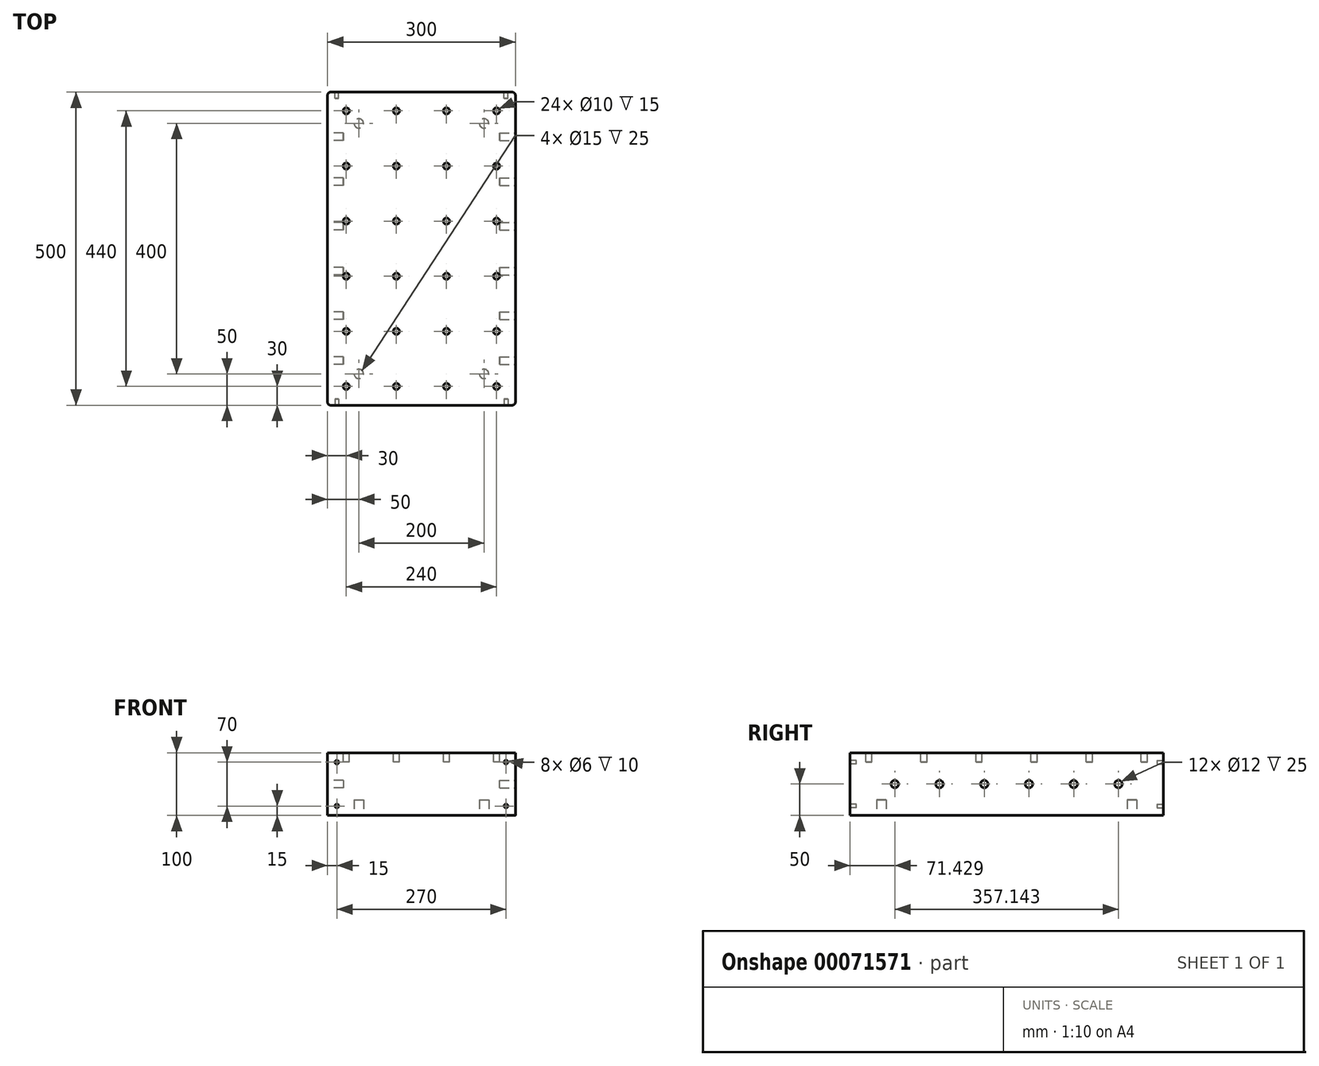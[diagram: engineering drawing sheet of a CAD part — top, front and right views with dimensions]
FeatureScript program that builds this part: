
annotation { "Feature Type Name" : "Feature", "Feature Type Description" : "" }
export const myFeature = defineFeature(function(context is Context, id is Id, definition is map)
    precondition{}
    {
        {
            var Q0;
            Q0=qCreatedBy(makeId("Top.planeOp"),FACE);
            var sketch = newSketch(context, id + "F0", { "sketchPlane" : qUnion([Q0])});
            skLineSegment(sketch, "E0.rect.bottom", {"start": v(-150, -250) * mm, "end": v(150, -250) * mm});
            skLineSegment(sketch, "E0.rect.top", {"start": v(-150, 250) * mm, "end": v(150, 250) * mm});
            skLineSegment(sketch, "E0.rect.left", {"start": v(-150, -250) * mm, "end": v(-150, 250) * mm});
            skLineSegment(sketch, "E0.rect.right", {"start": v(150, -250) * mm, "end": v(150, 250) * mm});
            skPoint(sketch, "E0.rect.middle", {"position": v(0, 0) * mm});
            skSolve(sketch);
        }
        {
            var Q0;
            Q0 = qSketchRegion(id + "F0", true);
            extrude(context, id + "F1", {"entities" : qUnion([Q0]), "depth" : 100 * mm});
        }
        {
            var Q0;
            Q0=makeQuery(id+"F1.opExtrude","CAP_FACE",FACE,{"disambiguationData":[OSD([sQuery(id+"F0.wireOp",EDGE,"E0.rect.bottom"),sQuery(id+"F0.wireOp",EDGE,"E0.rect.top"),sQuery(id+"F0.wireOp",EDGE,"E0.rect.left"),sQuery(id+"F0.wireOp",EDGE,"E0.rect.right")])],"isStart":true});
            var sketch = newSketch(context, id + "F2", { "sketchPlane" : qUnion([Q0])});
            skLineSegment(sketch, "E1.rect.bottom", {"start": v(-100, 200) * mm, "end": v(100, 200) * mm, "construction": true});
            skLineSegment(sketch, "E1.rect.top", {"start": v(-100, -200) * mm, "end": v(100, -200) * mm, "construction": true});
            skLineSegment(sketch, "E1.rect.left", {"start": v(-100, 200) * mm, "end": v(-100, -200) * mm, "construction": true});
            skLineSegment(sketch, "E1.rect.right", {"start": v(100, 200) * mm, "end": v(100, -200) * mm, "construction": true});
            skPoint(sketch, "E1.rect.middle", {"position": v(0, 0) * mm});
            skCircle(sketch, "E2", {"center": v(-100, 200) * mm, "radius": 7.5 * mm});
            skCircle(sketch, "E3", {"center": v(100, 200) * mm, "radius": 7.5 * mm});
            skCircle(sketch, "E4", {"center": v(100, -200) * mm, "radius": 7.5 * mm});
            skCircle(sketch, "E5", {"center": v(-100, -200) * mm, "radius": 7.5 * mm});
            skSolve(sketch);
        }
        {
            var Q0;
            Q0=qCreatedBy(makeId("Front.planeOp"),FACE);
            var sketch = newSketch(context, id + "F3", { "sketchPlane" : qUnion([Q0])});
            skLineSegment(sketch, "E6", {"start": v(150, 82.5) * mm, "end": v(150, 17.5) * mm});
            skLineSegment(sketch, "E7", {"start": v(150, 17.5) * mm, "end": v(120, 17.5) * mm});
            skLineSegment(sketch, "E8", {"start": v(120, 17.5) * mm, "end": v(120, 32.5) * mm});
            skLineSegment(sketch, "E9", {"start": v(120, 32.5) * mm, "end": v(140, 32.5) * mm});
            skLineSegment(sketch, "E10", {"start": v(140, 32.5) * mm, "end": v(140, 67.5) * mm});
            skLineSegment(sketch, "E11", {"start": v(140, 67.5) * mm, "end": v(120, 67.5) * mm});
            skLineSegment(sketch, "E12", {"start": v(120, 67.5) * mm, "end": v(120, 82.5) * mm});
            skLineSegment(sketch, "E13", {"start": v(120, 82.5) * mm, "end": v(150, 82.5) * mm});
            skLineSegment(sketch, "E14", {"start": v(150, 50) * mm, "end": v(120, 50) * mm, "construction": true});
            skLineSegment(sketch, "E15", {"start": v(120, 50) * mm, "end": v(120, 67.5) * mm, "construction": true});
            skLineSegment(sketch, "E16", {"start": v(120, 50) * mm, "end": v(120, 32.5) * mm, "construction": true});
            skLineSegment(sketch, "E17", {"start": v(0, 0) * mm, "end": v(0, 100) * mm, "construction": true});
            skLineSegment(sketch, "E18.MirrorCS", {"start": v(-150, 82.5) * mm, "end": v(-150, 17.5) * mm});
            skLineSegment(sketch, "E19.MirrorCS", {"start": v(-120, 50) * mm, "end": v(-120, 32.5) * mm, "construction": true});
            skLineSegment(sketch, "E20.MirrorCS", {"start": v(-140, 32.5) * mm, "end": v(-140, 67.5) * mm});
            skLineSegment(sketch, "E21.MirrorCS", {"start": v(-140, 67.5) * mm, "end": v(-120, 67.5) * mm});
            skLineSegment(sketch, "E22.MirrorCS", {"start": v(-120, 32.5) * mm, "end": v(-140, 32.5) * mm});
            skLineSegment(sketch, "E23.MirrorCS", {"start": v(-120, 82.5) * mm, "end": v(-150, 82.5) * mm});
            skLineSegment(sketch, "E24.MirrorCS", {"start": v(-120, 17.5) * mm, "end": v(-120, 32.5) * mm});
            skLineSegment(sketch, "E25.MirrorCS", {"start": v(-120, 67.5) * mm, "end": v(-120, 82.5) * mm});
            skLineSegment(sketch, "E26.MirrorCS", {"start": v(-150, 50) * mm, "end": v(-120, 50) * mm, "construction": true});
            skLineSegment(sketch, "E27.MirrorCS", {"start": v(-120, 50) * mm, "end": v(-120, 67.5) * mm, "construction": true});
            skLineSegment(sketch, "E28.MirrorCS", {"start": v(-150, 17.5) * mm, "end": v(-120, 17.5) * mm});
            skSolve(sketch);
        }
        {
            var Q0;
            Q0 = qSketchRegion(id + "F3", true);
            extrude(context, id + "F4", {"entities" : qUnion([Q0]), "operationType" : NewBodyOperationType.REMOVE, "oppositeDirection" : true, "depth" : 225 * mm, "hasSecondDirection" : true, "secondDirectionOppositeDirection" : false, "secondDirectionDepth" : 225 * mm});
        }
        {
            var Q0;
            Q0 = qSketchRegion(id + "F3", true);
            extrude(context, id + "F5", {"entities" : qUnion([Q0]), "operationType" : NewBodyOperationType.ADD, "depth" : 225 * mm, "hasSecondDirection" : true, "secondDirectionOppositeDirection" : true, "secondDirectionDepth" : 225 * mm});
        }
        {
            var Q0;
            Q0 = qSketchRegion(id + "F2", true);
            extrude(context, id + "F6", {"entities" : qUnion([Q0]), "operationType" : NewBodyOperationType.REMOVE, "oppositeDirection" : true, "depth" : 25 * mm});
        }
        {
            var Q0;
            Q0=makeQuery(id+"F1.opExtrude","SWEPT_FACE",FACE,{"disambiguationData":[OSD([sQuery(id+"F0.wireOp",EDGE,"E0.rect.left")])]});
            var sketch = newSketch(context, id + "F7", { "sketchPlane" : qUnion([Q0])});
            skLineSegment(sketch, "E29", {"start": v(-250, 50) * mm, "end": v(-178.57, 50) * mm, "construction": true});
            skLineSegment(sketch, "E30", {"start": v(-178.57, 50) * mm, "end": v(-107.14, 50) * mm, "construction": true});
            skLineSegment(sketch, "E31", {"start": v(-107.14, 50) * mm, "end": v(-35.71, 50) * mm, "construction": true});
            skLineSegment(sketch, "E32", {"start": v(-35.71, 50) * mm, "end": v(35.71, 50) * mm, "construction": true});
            skLineSegment(sketch, "E33", {"start": v(35.71, 50) * mm, "end": v(107.14, 50) * mm, "construction": true});
            skLineSegment(sketch, "E34", {"start": v(107.14, 50) * mm, "end": v(178.57, 50) * mm, "construction": true});
            skLineSegment(sketch, "E35", {"start": v(178.57, 50) * mm, "end": v(250, 50) * mm, "construction": true});
            skCircle(sketch, "E36", {"center": v(-178.57, 50) * mm, "radius": 6 * mm});
            skCircle(sketch, "E37", {"center": v(-107.14, 50) * mm, "radius": 6 * mm});
            skCircle(sketch, "E38", {"center": v(-35.71, 50) * mm, "radius": 6 * mm});
            skCircle(sketch, "E39", {"center": v(35.71, 50) * mm, "radius": 6 * mm});
            skCircle(sketch, "E40", {"center": v(107.14, 50) * mm, "radius": 6 * mm});
            skCircle(sketch, "E41", {"center": v(178.57, 50) * mm, "radius": 6 * mm});
            skSolve(sketch);
        }
        {
            var Q0;
            Q0 = qSketchRegion(id + "F7", true);
            extrude(context, id + "F8", {"entities" : qUnion([Q0]), "operationType" : NewBodyOperationType.REMOVE, "oppositeDirection" : true, "depth" : 25 * mm});
        }
        {
            var Q0;
            Q0=makeQuery(id+"F1.opExtrude","SWEPT_FACE",FACE,{"disambiguationData":[OSD([sQuery(id+"F0.wireOp",EDGE,"E0.rect.right")])]});
            var sketch = newSketch(context, id + "F9", { "sketchPlane" : qUnion([Q0])});
            skLineSegment(sketch, "E42", {"start": v(-250, 50) * mm, "end": v(-178.57, 50) * mm, "construction": true});
            skLineSegment(sketch, "E43", {"start": v(-178.57, 50) * mm, "end": v(-107.14, 50) * mm, "construction": true});
            skLineSegment(sketch, "E44", {"start": v(-107.14, 50) * mm, "end": v(-35.71, 50) * mm, "construction": true});
            skLineSegment(sketch, "E45", {"start": v(-35.71, 50) * mm, "end": v(35.71, 50) * mm, "construction": true});
            skLineSegment(sketch, "E46", {"start": v(35.71, 50) * mm, "end": v(107.14, 50) * mm, "construction": true});
            skLineSegment(sketch, "E47", {"start": v(107.14, 50) * mm, "end": v(178.57, 50) * mm, "construction": true});
            skLineSegment(sketch, "E48", {"start": v(178.57, 50) * mm, "end": v(250, 50) * mm, "construction": true});
            skCircle(sketch, "E49", {"center": v(-178.57, 50) * mm, "radius": 6 * mm});
            skCircle(sketch, "E50", {"center": v(-107.14, 50) * mm, "radius": 6 * mm});
            skCircle(sketch, "E51", {"center": v(-35.71, 50) * mm, "radius": 6 * mm});
            skCircle(sketch, "E52", {"center": v(35.71, 50) * mm, "radius": 6 * mm});
            skCircle(sketch, "E53", {"center": v(107.14, 50) * mm, "radius": 6 * mm});
            skCircle(sketch, "E54", {"center": v(178.57, 50) * mm, "radius": 6 * mm});
            skSolve(sketch);
        }
        {
            var Q0;
            Q0=makeQuery(id+"F9.imprint","IMPRINT",FACE,{"disambiguationData":[TD([[makeQuery(id+"F9.imprint","IMPRINT",EDGE,{"derivedFrom":sQuery(id+"F9.wireOp",EDGE,"E49")}),1.0]])]});
            var Q1;
            Q1=makeQuery(id+"F9.imprint","IMPRINT",FACE,{"disambiguationData":[TD([[makeQuery(id+"F9.imprint","IMPRINT",EDGE,{"derivedFrom":sQuery(id+"F9.wireOp",EDGE,"E50")}),1.0]])]});
            var Q2;
            Q2=makeQuery(id+"F9.imprint","IMPRINT",FACE,{"disambiguationData":[TD([[makeQuery(id+"F9.imprint","IMPRINT",EDGE,{"derivedFrom":sQuery(id+"F9.wireOp",EDGE,"E51")}),1.0]])]});
            var Q3;
            Q3=makeQuery(id+"F9.imprint","IMPRINT",FACE,{"disambiguationData":[TD([[makeQuery(id+"F9.imprint","IMPRINT",EDGE,{"derivedFrom":sQuery(id+"F9.wireOp",EDGE,"E52")}),1.0]])]});
            var Q4;
            Q4=makeQuery(id+"F9.imprint","IMPRINT",FACE,{"disambiguationData":[TD([[makeQuery(id+"F9.imprint","IMPRINT",EDGE,{"derivedFrom":sQuery(id+"F9.wireOp",EDGE,"E53")}),1.0]])]});
            var Q5;
            Q5=makeQuery(id+"F9.imprint","IMPRINT",FACE,{"disambiguationData":[TD([[makeQuery(id+"F9.imprint","IMPRINT",EDGE,{"derivedFrom":sQuery(id+"F9.wireOp",EDGE,"E54")}),1.0]])]});
            extrude(context, id + "F10", {"entities" : qUnion([Q0, Q1, Q2, Q3, Q4, Q5]), "operationType" : NewBodyOperationType.REMOVE, "oppositeDirection" : true, "depth" : 25 * mm});
        }
        {
            var Q0;
            Q0=makeQuery(id+"F1.opExtrude","SWEPT_FACE",FACE,{"disambiguationData":[OSD([sQuery(id+"F0.wireOp",EDGE,"E0.rect.top")])]});
            var sketch = newSketch(context, id + "F11", { "sketchPlane" : qUnion([Q0])});
            skLineSegment(sketch, "E55.bottom", {"start": v(-135, 85) * mm, "end": v(135, 85) * mm, "construction": true});
            skLineSegment(sketch, "E55.top", {"start": v(-135, 15) * mm, "end": v(135, 15) * mm, "construction": true});
            skLineSegment(sketch, "E55.left", {"start": v(-135, 85) * mm, "end": v(-135, 15) * mm, "construction": true});
            skLineSegment(sketch, "E55.right", {"start": v(135, 85) * mm, "end": v(135, 15) * mm, "construction": true});
            skCircle(sketch, "E56", {"center": v(-135, 85) * mm, "radius": 3 * mm});
            skCircle(sketch, "E57", {"center": v(-135, 15) * mm, "radius": 3 * mm});
            skCircle(sketch, "E58", {"center": v(135, 15) * mm, "radius": 3 * mm});
            skCircle(sketch, "E59", {"center": v(135, 85) * mm, "radius": 3 * mm});
            skLineSegment(sketch, "E60", {"start": v(-150, 50) * mm, "end": v(-135, 50) * mm, "construction": true});
            skLineSegment(sketch, "E61", {"start": v(0, 0) * mm, "end": v(0, 15) * mm, "construction": true});
            skLineSegment(sketch, "E62", {"start": v(135, 50) * mm, "end": v(150, 50) * mm, "construction": true});
            skSolve(sketch);
        }
        {
            var Q0;
            Q0 = qSketchRegion(id + "F11", true);
            extrude(context, id + "F12", {"entities" : qUnion([Q0]), "operationType" : NewBodyOperationType.REMOVE, "oppositeDirection" : true, "depth" : 10 * mm});
        }
        {
            var Q0;
            Q0=makeQuery(id+"F1.opExtrude","SWEPT_FACE",FACE,{"disambiguationData":[OSD([sQuery(id+"F0.wireOp",EDGE,"E0.rect.bottom")])]});
            var sketch = newSketch(context, id + "F13", { "sketchPlane" : qUnion([Q0])});
            skLineSegment(sketch, "E63.right", {"start": v(135, 85) * mm, "end": v(135, 15) * mm, "construction": true});
            skLineSegment(sketch, "E63.left", {"start": v(-135, 85) * mm, "end": v(-135, 15) * mm, "construction": true});
            skLineSegment(sketch, "E63.top", {"start": v(-135, 15) * mm, "end": v(135, 15) * mm, "construction": true});
            skLineSegment(sketch, "E63.bottom", {"start": v(-135, 85) * mm, "end": v(135, 85) * mm, "construction": true});
            skCircle(sketch, "E64", {"center": v(135, 85) * mm, "radius": 3 * mm});
            skCircle(sketch, "E65", {"center": v(135, 15) * mm, "radius": 3 * mm});
            skCircle(sketch, "E66", {"center": v(-135, 15) * mm, "radius": 3 * mm});
            skCircle(sketch, "E67", {"center": v(-135, 85) * mm, "radius": 3 * mm});
            skLineSegment(sketch, "E68", {"start": v(0, 85) * mm, "end": v(0, 100) * mm});
            skLineSegment(sketch, "E69", {"start": v(135, 50) * mm, "end": v(150, 50) * mm});
            skLineSegment(sketch, "E70", {"start": v(0, 0) * mm, "end": v(0, 15) * mm});
            skLineSegment(sketch, "E71", {"start": v(-135, 50) * mm, "end": v(-150, 50) * mm});
            skSolve(sketch);
        }
        {
            var Q0;
            Q0 = qSketchRegion(id + "F13", true);
            extrude(context, id + "F14", {"entities" : qUnion([Q0]), "operationType" : NewBodyOperationType.REMOVE, "oppositeDirection" : true, "depth" : 10 * mm});
        }
        {
            var Q0;
            Q0=makeQuery(id+"F1.opExtrude","CAP_FACE",FACE,{"disambiguationData":[OSD([sQuery(id+"F0.wireOp",EDGE,"E0.rect.bottom"),sQuery(id+"F0.wireOp",EDGE,"E0.rect.top"),sQuery(id+"F0.wireOp",EDGE,"E0.rect.left"),sQuery(id+"F0.wireOp",EDGE,"E0.rect.right")])],"isStart":false});
            var sketch = newSketch(context, id + "F15", { "sketchPlane" : qUnion([Q0])});
            skLineSegment(sketch, "E72.rect.bottom", {"start": v(-120, 220) * mm, "end": v(120, 220) * mm, "construction": true});
            skLineSegment(sketch, "E72.rect.top", {"start": v(-120, -220) * mm, "end": v(120, -220) * mm, "construction": true});
            skLineSegment(sketch, "E72.rect.left", {"start": v(-120, 220) * mm, "end": v(-120, -220) * mm, "construction": true});
            skLineSegment(sketch, "E72.rect.right", {"start": v(120, 220) * mm, "end": v(120, -220) * mm, "construction": true});
            skPoint(sketch, "E72.rect.middle", {"position": v(0, 0) * mm});
            skLineSegment(sketch, "E73", {"start": v(0, 220) * mm, "end": v(0, 250) * mm, "construction": true});
            skLineSegment(sketch, "E74", {"start": v(120, 0) * mm, "end": v(150, 0) * mm, "construction": true});
            skCircle(sketch, "E75", {"center": v(120, 220) * mm, "radius": 5 * mm});
            skCircle(sketch, "E76.0.1.0", {"center": v(120, 132) * mm, "radius": 5 * mm});
            skCircle(sketch, "E76.0.2.0", {"center": v(120, 44) * mm, "radius": 5 * mm});
            skCircle(sketch, "E76.0.3.0", {"center": v(120, -44) * mm, "radius": 5 * mm});
            skCircle(sketch, "E76.0.4.0", {"center": v(120, -132) * mm, "radius": 5 * mm});
            skCircle(sketch, "E76.0.5.0", {"center": v(120, -220) * mm, "radius": 5 * mm});
            skCircle(sketch, "E76.1.0.0", {"center": v(40, 220) * mm, "radius": 5 * mm});
            skCircle(sketch, "E76.1.1.0", {"center": v(40, 132) * mm, "radius": 5 * mm});
            skCircle(sketch, "E76.1.2.0", {"center": v(40, 44) * mm, "radius": 5 * mm});
            skCircle(sketch, "E76.1.3.0", {"center": v(40, -44) * mm, "radius": 5 * mm});
            skCircle(sketch, "E76.1.4.0", {"center": v(40, -132) * mm, "radius": 5 * mm});
            skCircle(sketch, "E76.1.5.0", {"center": v(40, -220) * mm, "radius": 5 * mm});
            skCircle(sketch, "E76.2.0.0", {"center": v(-40, 220) * mm, "radius": 5 * mm});
            skCircle(sketch, "E76.2.1.0", {"center": v(-40, 132) * mm, "radius": 5 * mm});
            skCircle(sketch, "E76.2.2.0", {"center": v(-40, 44) * mm, "radius": 5 * mm});
            skCircle(sketch, "E76.2.3.0", {"center": v(-40, -44) * mm, "radius": 5 * mm});
            skCircle(sketch, "E76.2.4.0", {"center": v(-40, -132) * mm, "radius": 5 * mm});
            skCircle(sketch, "E76.2.5.0", {"center": v(-40, -220) * mm, "radius": 5 * mm});
            skCircle(sketch, "E76.3.0.0", {"center": v(-120, 220) * mm, "radius": 5 * mm});
            skCircle(sketch, "E76.3.1.0", {"center": v(-120, 132) * mm, "radius": 5 * mm});
            skCircle(sketch, "E76.3.2.0", {"center": v(-120, 44) * mm, "radius": 5 * mm});
            skCircle(sketch, "E76.3.3.0", {"center": v(-120, -44) * mm, "radius": 5 * mm});
            skCircle(sketch, "E76.3.4.0", {"center": v(-120, -132) * mm, "radius": 5 * mm});
            skCircle(sketch, "E76.3.5.0", {"center": v(-120, -220) * mm, "radius": 5 * mm});
            skLineSegment(sketch, "E76.direction1", {"start": v(120, 220) * mm, "end": v(40, 220) * mm, "construction": true});
            skLineSegment(sketch, "E76.direction2", {"start": v(120, 220) * mm, "end": v(120, 132) * mm, "construction": true});
            skSolve(sketch);
        }
        {
            var Q0;
            Q0 = qSketchRegion(id + "F15", true);
            extrude(context, id + "F16", {"entities" : qUnion([Q0]), "operationType" : NewBodyOperationType.REMOVE, "oppositeDirection" : true, "depth" : 15 * mm});
        }
        {
            var Q0;
            Q0=makeQuery(id+"F1.opExtrude","SWEPT_EDGE",EDGE,{"disambiguationData":[OSD([sQuery(id+"F0.wireOp",EDGE,"E0.rect.top"),sQuery(id+"F0.wireOp",EDGE,"E0.rect.right")])]});
            var Q1;
            Q1=makeQuery(id+"F1.opExtrude","SWEPT_EDGE",EDGE,{"disambiguationData":[OSD([sQuery(id+"F0.wireOp",EDGE,"E0.rect.top"),sQuery(id+"F0.wireOp",EDGE,"E0.rect.left")])]});
            var Q2;
            Q2=makeQuery(id+"F1.opExtrude","SWEPT_EDGE",EDGE,{"disambiguationData":[OSD([sQuery(id+"F0.wireOp",EDGE,"E0.rect.bottom"),sQuery(id+"F0.wireOp",EDGE,"E0.rect.left")])]});
            var Q3;
            Q3=makeQuery(id+"F1.opExtrude","SWEPT_EDGE",EDGE,{"disambiguationData":[OSD([sQuery(id+"F0.wireOp",EDGE,"E0.rect.bottom"),sQuery(id+"F0.wireOp",EDGE,"E0.rect.right")])]});
            fillet(context, id + "F17", {"entities" : qUnion([Q0, Q1, Q2, Q3]), "radius" : 5 * mm, "tangentPropagation" : true, "allowEdgeOverflow" : false});
        }
    });
